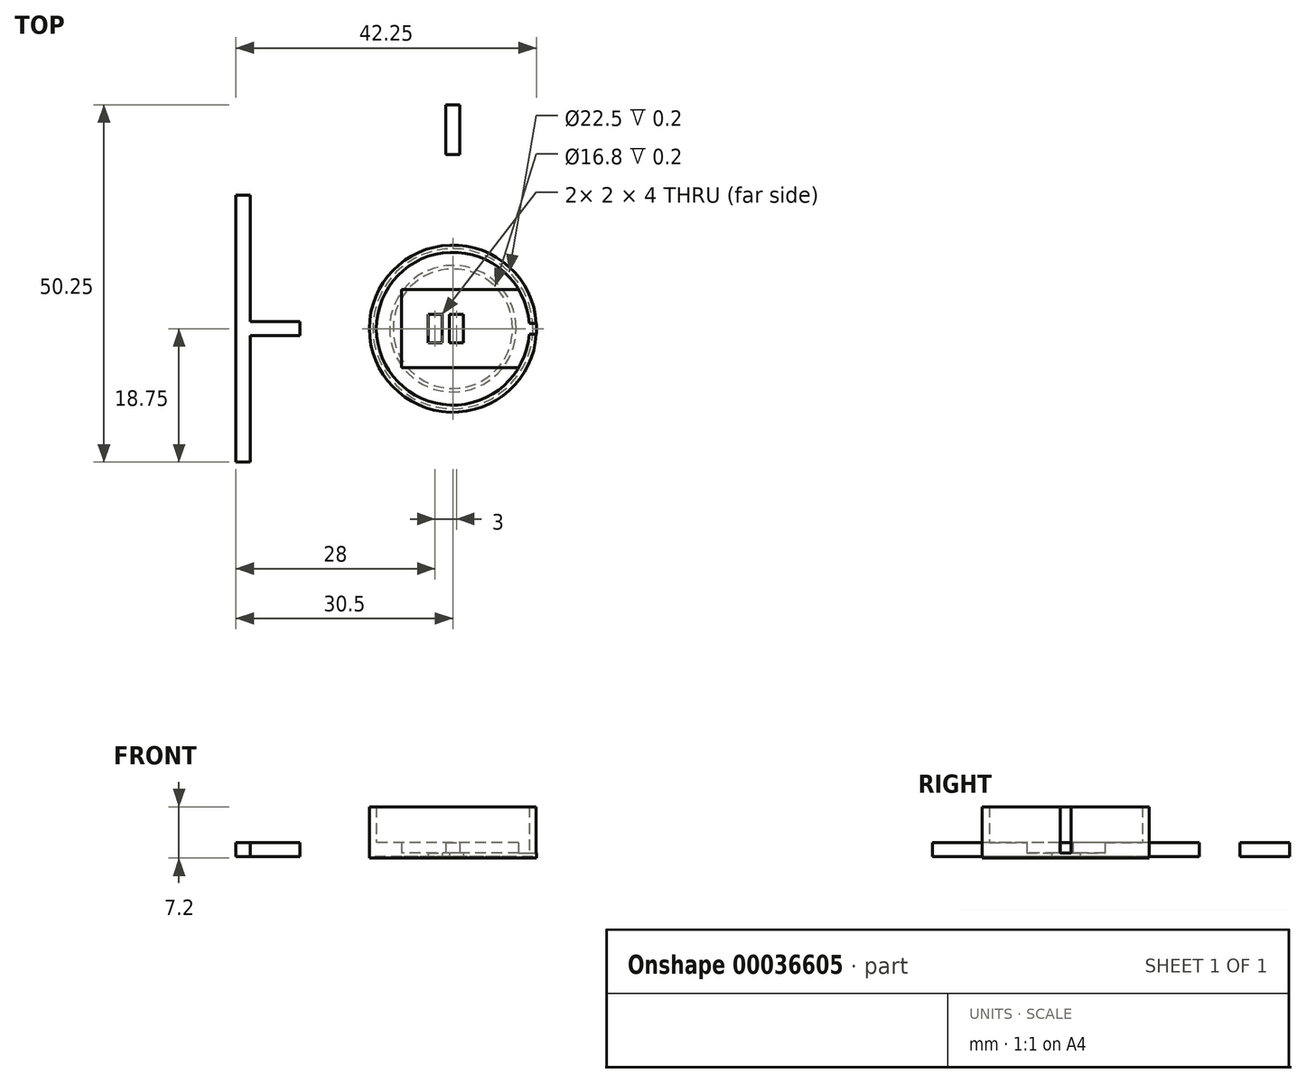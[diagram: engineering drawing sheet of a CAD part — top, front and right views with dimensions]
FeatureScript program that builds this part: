
annotation { "Feature Type Name" : "Feature", "Feature Type Description" : "" }
export const myFeature = defineFeature(function(context is Context, id is Id, definition is map)
    precondition{}
    {
        {
            var Q0;
            Q0=qCreatedBy(makeId("Top.planeOp"),FACE);
            var sketch = newSketch(context, id + "F0", { "sketchPlane" : qUnion([Q0])});
            skCircle(sketch, "E0", {"center": v(0, 0) * mm, "radius": 10.75 * mm});
            skCircle(sketch, "E1", {"center": v(0, 0) * mm, "radius": 11.75 * mm});
            skLineSegment(sketch, "E2.rect.bottom", {"start": v(7.25, 5.5) * mm, "end": v(-7.25, 5.5) * mm});
            skLineSegment(sketch, "E2.rect.top", {"start": v(7.25, -5.5) * mm, "end": v(-7.25, -5.5) * mm});
            skLineSegment(sketch, "E2.rect.left", {"start": v(7.25, 5.5) * mm, "end": v(7.25, -5.5) * mm});
            skLineSegment(sketch, "E2.rect.right", {"start": v(-7.25, 5.5) * mm, "end": v(-7.25, -5.5) * mm});
            skLineSegment(sketch, "E3", {"start": v(-1, 0) * mm, "end": v(-1, 15.97) * mm, "construction": true});
            skPoint(sketch, "E4.rect.middle", {"position": v(-1, 0) * mm});
            skLineSegment(sketch, "E5.rect.bottom", {"start": v(-3.5, 2) * mm, "end": v(-1.5, 2) * mm});
            skLineSegment(sketch, "E5.rect.top", {"start": v(-3.5, -2) * mm, "end": v(-1.5, -2) * mm});
            skLineSegment(sketch, "E5.rect.left", {"start": v(-3.5, 2) * mm, "end": v(-3.5, -2) * mm});
            skLineSegment(sketch, "E5.rect.right", {"start": v(-1.5, 2) * mm, "end": v(-1.5, -2) * mm});
            skPoint(sketch, "E5.rect.middle", {"position": v(-2.5, 0) * mm});
            skLineSegment(sketch, "E6.MirrorCS", {"start": v(-0.5, 2) * mm, "end": v(-0.5, -2) * mm});
            skLineSegment(sketch, "E7.MirrorCS", {"start": v(1.5, 2) * mm, "end": v(-0.5, 2) * mm});
            skLineSegment(sketch, "E8.MirrorCS", {"start": v(1.5, 2) * mm, "end": v(1.5, -2) * mm});
            skLineSegment(sketch, "E9.MirrorCS", {"start": v(1.5, -2) * mm, "end": v(-0.5, -2) * mm});
            skLineSegment(sketch, "E10", {"start": v(7.25, -5.5) * mm, "end": v(9.24, -5.5) * mm});
            skLineSegment(sketch, "E11", {"start": v(7.25, 5.5) * mm, "end": v(9.24, 5.5) * mm});
            skLineSegment(sketch, "E12", {"start": v(-1, 0) * mm, "end": v(21.2, 0) * mm, "construction": true});
            skLineSegment(sketch, "E13", {"start": v(10.72, 0.75) * mm, "end": v(11.73, 0.75) * mm});
            skLineSegment(sketch, "E14.MirrorCS", {"start": v(10.72, -0.75) * mm, "end": v(11.73, -0.75) * mm});
            skSolve(sketch);
        }
        {
            var Q0;
            Q0=makeQuery(id+"F0.imprint","IMPRINT",FACE,{"disambiguationData":[TD([[makeQuery(id+"F0.imprint","IMPRINT",EDGE,{"derivedFrom":sQuery(id+"F0.wireOp",EDGE,"E2.rect.bottom")}),-1.0]])]});
            var sketch = newSketch(context, id + "F1", { "sketchPlane" : qUnion([Q0])});
            skCircle(sketch, "E15", {"center": v(0, 0) * mm, "radius": 11.75 * mm});
            skCircle(sketch, "E16", {"center": v(0, 0) * mm, "radius": 8.9 * mm});
            skCircle(sketch, "E17.0", {"center": v(0, 0) * mm, "radius": 11.25 * mm});
            skCircle(sketch, "E18.0", {"center": v(0, 0) * mm, "radius": 8.4 * mm});
            skSolve(sketch);
        }
        {
            var Q0;
            {var subQ1=sQuery(id+"F0.wireOp",EDGE,"E13");Q0=makeQuery(id+"F0.imprint","IMPRINT",FACE,{"disambiguationData":[TD([[makeQuery(id+"F0.imprint","IMPRINT",EDGE,{"derivedFrom":subQ1}),1.0]])]});}
            extrude(context, id + "F2", {"entities" : qUnion([Q0]), "depth" : 7 * mm});
        }
        {
            var Q0;
            Q0=makeQuery(id+"F0.imprint","IMPRINT",FACE,{"disambiguationData":[TD([[makeQuery(id+"F0.imprint","IMPRINT",EDGE,{"derivedFrom":sQuery(id+"F0.wireOp",EDGE,"E2.rect.bottom")}),-1.0]])]});
            extrude(context, id + "F3", {"entities" : qUnion([Q0]), "operationType" : NewBodyOperationType.ADD, "depth" : 2 * mm});
        }
        {
            var Q0;
            Q0=makeQuery(id+"F0.imprint","IMPRINT",FACE,{"disambiguationData":[TD([[makeQuery(id+"F0.imprint","IMPRINT",EDGE,{"derivedFrom":sQuery(id+"F0.wireOp",EDGE,"E2.rect.bottom")}),1.0]])]});
            extrude(context, id + "F4", {"entities" : qUnion([Q0]), "operationType" : NewBodyOperationType.ADD, "depth" : 0.5 * mm});
        }
        {
            var Q0;
            Q0=makeQuery(id+"F0.imprint","IMPRINT",FACE,{"disambiguationData":[TD([[makeQuery(id+"F0.imprint","IMPRINT",EDGE,{"derivedFrom":sQuery(id+"F0.wireOp",EDGE,"E2.rect.left")}),1.0]])]});
            var Q1;
            {var subQ1=sQuery(id+"F0.wireOp",EDGE,"E13");Q1=makeQuery(id+"F0.imprint","IMPRINT",FACE,{"disambiguationData":[TD([[makeQuery(id+"F0.imprint","IMPRINT",EDGE,{"derivedFrom":subQ1}),-1.0]])]});}
            extrude(context, id + "F5", {"entities" : qUnion([Q0, Q1]), "operationType" : NewBodyOperationType.ADD, "depth" : 0.5 * mm});
        }
        {
            var Q0;
            Q0=makeQuery(id+"F1.imprint","IMPRINT",FACE,{"disambiguationData":[TD([[makeQuery(id+"F1.imprint","IMPRINT",EDGE,{"derivedFrom":sQuery(id+"F1.wireOp",EDGE,"E15")}),1.0]])]});
            var Q1;
            {var subQ3=sQuery(id+"F1.wireOp",EDGE,"E16");var subQ5=makeQuery(id+"F0.imprint","IMPRINT",EDGE,{"derivedFrom":sQuery(id+"F0.wireOp",EDGE,"E2.rect.bottom")});var subQ7=makeQuery(id+"F1.imprint","INTERSECT",VERTEX,{"disambiguationData":[OD(1.0)],"derivedFrom":[subQ5,subQ3]});Q1=makeQuery(id+"F1.imprint","IMPRINT",FACE,{"disambiguationData":[TD([[makeQuery(id+"F1.imprint","IMPRINT",EDGE,{"disambiguationData":[TD([[subQ7,1.0]])],"derivedFrom":subQ3}),1.0]])]});}
            var Q2;
            {var subQ0=makeQuery(id+"F0.imprint","IMPRINT",EDGE,{"derivedFrom":sQuery(id+"F0.wireOp",EDGE,"E2.rect.top")});var subQ3=sQuery(id+"F1.wireOp",EDGE,"E16");var subQ6=makeQuery(id+"F1.imprint","INTERSECT",VERTEX,{"disambiguationData":[OD(0.0)],"derivedFrom":[subQ0,subQ3]});Q2=makeQuery(id+"F1.imprint","IMPRINT",FACE,{"disambiguationData":[TD([[makeQuery(id+"F1.imprint","IMPRINT",EDGE,{"disambiguationData":[TD([[subQ6,-1.0]])],"derivedFrom":subQ3}),1.0]])]});}
            var Q3;
            {var subQ0=makeQuery(id+"F0.imprint","IMPRINT",EDGE,{"derivedFrom":sQuery(id+"F0.wireOp",EDGE,"E2.rect.right")});var subQ3=sQuery(id+"F1.wireOp",EDGE,"E16");var subQ4=makeQuery(id+"F1.imprint","INTERSECT",VERTEX,{"disambiguationData":[OD(1.0)],"derivedFrom":[subQ0,subQ3]});Q3=makeQuery(id+"F1.imprint","IMPRINT",FACE,{"disambiguationData":[TD([[makeQuery(id+"F1.imprint","IMPRINT",EDGE,{"disambiguationData":[TD([[subQ4,-1.0]])],"derivedFrom":subQ3}),1.0]])]});}
            var Q4;
            {var subQ0=makeQuery(id+"F0.imprint","IMPRINT",EDGE,{"derivedFrom":sQuery(id+"F0.wireOp",EDGE,"E2.rect.right")});var subQ3=sQuery(id+"F1.wireOp",EDGE,"E16");var subQ6=makeQuery(id+"F1.imprint","INTERSECT",VERTEX,{"disambiguationData":[OD(0.0)],"derivedFrom":[subQ0,subQ3]});Q4=makeQuery(id+"F1.imprint","IMPRINT",FACE,{"disambiguationData":[TD([[makeQuery(id+"F1.imprint","IMPRINT",EDGE,{"disambiguationData":[TD([[subQ6,-1.0]])],"derivedFrom":subQ3}),1.0]])]});}
            var Q5;
            {var subQ0=makeQuery(id+"F0.imprint","IMPRINT",EDGE,{"derivedFrom":sQuery(id+"F0.wireOp",EDGE,"E2.rect.bottom")});var subQ3=sQuery(id+"F1.wireOp",EDGE,"E16");var subQ6=makeQuery(id+"F1.imprint","INTERSECT",VERTEX,{"disambiguationData":[OD(0.0)],"derivedFrom":[subQ0,subQ3]});Q5=makeQuery(id+"F1.imprint","IMPRINT",FACE,{"disambiguationData":[TD([[makeQuery(id+"F1.imprint","IMPRINT",EDGE,{"disambiguationData":[TD([[subQ6,1.0]])],"derivedFrom":subQ3}),1.0]])]});}
            var Q6;
            {var subQ3=sQuery(id+"F1.wireOp",EDGE,"E16");var subQ5=makeQuery(id+"F0.imprint","IMPRINT",EDGE,{"derivedFrom":sQuery(id+"F0.wireOp",EDGE,"E2.rect.bottom")});var subQ7=makeQuery(id+"F1.imprint","INTERSECT",VERTEX,{"disambiguationData":[OD(0.0)],"derivedFrom":[subQ5,subQ3]});Q6=makeQuery(id+"F1.imprint","IMPRINT",FACE,{"disambiguationData":[TD([[makeQuery(id+"F1.imprint","IMPRINT",EDGE,{"disambiguationData":[TD([[subQ7,-1.0]])],"derivedFrom":subQ3}),1.0]])]});}
            extrude(context, id + "F6", {"entities" : qUnion([Q0, Q1, Q2, Q3, Q4, Q5, Q6]), "operationType" : NewBodyOperationType.ADD, "oppositeDirection" : true, "depth" : 0.2 * mm});
        }
        {
            var Q0;
            Q0=qCreatedBy(makeId("Top.planeOp"),FACE);
            var sketch = newSketch(context, id + "F7", { "sketchPlane" : qUnion([Q0])});
            skLineSegment(sketch, "E19.rect.bottom", {"start": v(-30.5, 18.75) * mm, "end": v(-28.5, 18.75) * mm});
            skLineSegment(sketch, "E19.rect.top", {"start": v(-30.5, -18.75) * mm, "end": v(-28.5, -18.75) * mm});
            skLineSegment(sketch, "E19.rect.left", {"start": v(-30.5, 18.75) * mm, "end": v(-30.5, -18.75) * mm});
            skLineSegment(sketch, "E19.rect.right", {"start": v(-28.5, 18.75) * mm, "end": v(-28.5, -18.75) * mm});
            skPoint(sketch, "E19.rect.middle", {"position": v(-29.5, 0) * mm});
            skLineSegment(sketch, "E20.rect.bottom", {"start": v(-21.5, 1) * mm, "end": v(-28.5, 1) * mm});
            skLineSegment(sketch, "E20.rect.top", {"start": v(-21.5, -1) * mm, "end": v(-28.5, -1) * mm});
            skLineSegment(sketch, "E20.rect.left", {"start": v(-21.5, 1) * mm, "end": v(-21.5, -1) * mm});
            skLineSegment(sketch, "E20.rect.right", {"start": v(-28.5, 1) * mm, "end": v(-28.5, -1) * mm});
            skPoint(sketch, "E20.rect.middle", {"position": v(-25, 0) * mm});
            skPoint(sketch, "E20.rect.middle.positionSnap0", {"position": v(-28.5, 0) * mm});
            skPoint(sketch, "E20.rect.centerSnap0", {"position": v(-28.5, 0) * mm});
            skLineSegment(sketch, "E21.rect.bottom", {"start": v(-1, 24.5) * mm, "end": v(1, 24.5) * mm});
            skLineSegment(sketch, "E21.rect.top", {"start": v(-1, 31.5) * mm, "end": v(1, 31.5) * mm});
            skLineSegment(sketch, "E21.rect.left", {"start": v(-1, 24.5) * mm, "end": v(-1, 31.5) * mm});
            skLineSegment(sketch, "E21.rect.right", {"start": v(1, 24.5) * mm, "end": v(1, 31.5) * mm});
            skPoint(sketch, "E21.rect.middle", {"position": v(0, 28) * mm});
            skSolve(sketch);
        }
        {
            var Q0;
            {var subQ3=sQuery(id+"F7.wireOp",EDGE,"E19.rect.bottom");Q0=makeQuery(id+"F7.imprint","IMPRINT",FACE,{"disambiguationData":[TD([[makeQuery(id+"F7.imprint","IMPRINT",EDGE,{"derivedFrom":subQ3}),-1.0]])]});}
            var Q1;
            Q1=makeQuery(id+"F7.imprint","IMPRINT",FACE,{"disambiguationData":[TD([[makeQuery(id+"F7.imprint","IMPRINT",EDGE,{"derivedFrom":sQuery(id+"F7.wireOp",EDGE,"E20.rect.bottom")}),1.0]])]});
            var Q2;
            Q2=makeQuery(id+"F7.imprint","IMPRINT",FACE,{"disambiguationData":[TD([[makeQuery(id+"F7.imprint","IMPRINT",EDGE,{"derivedFrom":sQuery(id+"F7.wireOp",EDGE,"E21.rect.bottom")}),1.0]])]});
            extrude(context, id + "F8", {"entities" : qUnion([Q0, Q1, Q2]), "depth" : 2 * mm});
        }
    });
